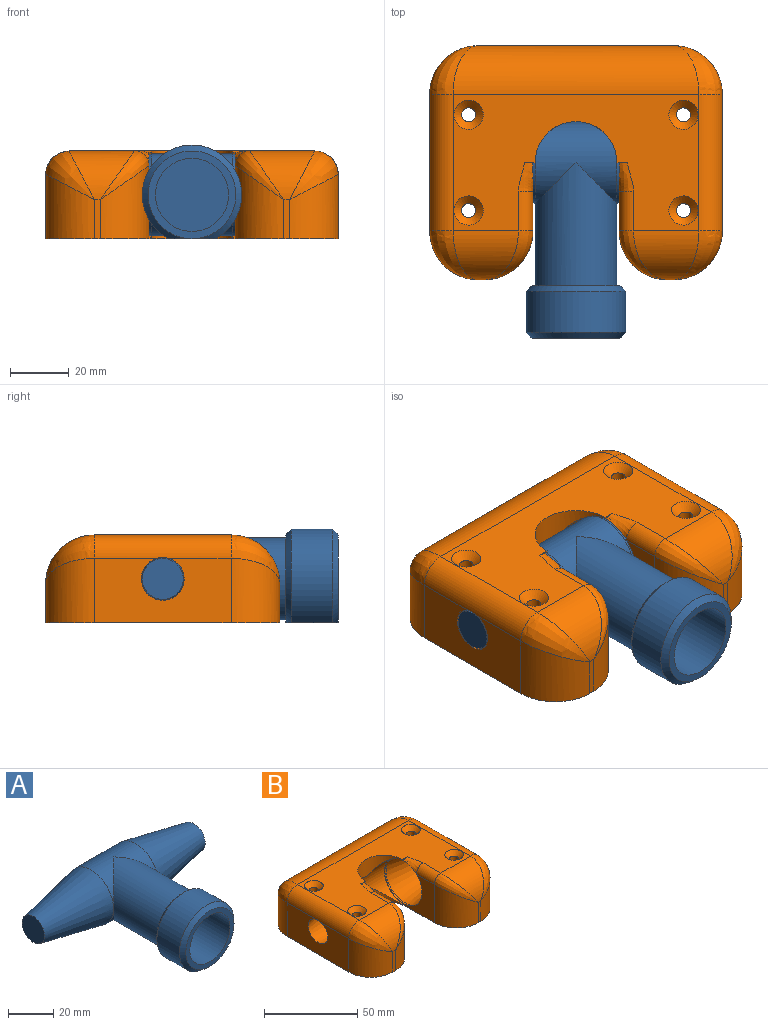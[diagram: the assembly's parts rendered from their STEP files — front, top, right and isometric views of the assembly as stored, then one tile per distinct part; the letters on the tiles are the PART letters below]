
ASSEMBLY  parts=2 mates=1
PART A: 14 faces, bbox 100x74x34 mm
  f0: cylinder r=17mm len=34mm, axis (0,1,0), area 1262.2mm2, adj f1,f2,f13
  f1: cone r=15mm half-angle=45deg, axis (0,-1,0), area 253.8mm2, adj f0,f10,f13
  f2: cone r=17mm half-angle=45deg, axis (0,1,0), area 253.8mm2, adj f0,f9,f13
  f3: cone r=7mm half-angle=11deg, axis (1,0,0), area 2419.5mm2, adj f4,f7
  f4: plane 14x14mm, normal (-1,0,0), area 153.9mm2, adj f3
  f5: plane 14x14mm, normal (1,0,0), area 153.9mm2, adj f6
  f6: cone r=7mm half-angle=11deg, axis (-1,0,0), area 2419.5mm2, adj f5,f7
  f7: cylinder r=14mm len=28mm, axis (-1,0,0), area 1679mm2, adj f3,f6,f8
  f8: cylinder r=14mm len=42mm, axis (0,1,0), area 2910.5mm2, adj f7,f10
  f9: plane 30x30mm, normal (0,-1,0), area 216mm2, adj f2,f11
  f10: plane 30x30mm, normal (0,1,0), area 91.1mm2, adj f1,f8
  f11: cylinder r=12.5mm len=34mm, axis (0,-1,0), area 2670.4mm2, adj f9,f12
  f12: plane 25x25mm, normal (0,-1,0), area 490.9mm2, adj f11
  f13: plane 18.01x16.02mm, normal (0,0,-1), area 266.1mm2, adj f0,f1,f2
PART B: 49 faces, bbox 100x80x30 mm
  f0: cylinder r=14mm len=28mm, axis (-1,0,0), area 76.7mm2, adj f13,f18,f45
  f1: cylinder r=14mm len=28mm, axis (0,0,1), area 222.5mm2, adj f2,f3,f5,f19
  f2: plane 3.71x1.01mm, normal (0,-1,0), area 1.3mm2, adj f1,f5,f13,f19,f45
  f3: plane 3.71x1.01mm, normal (0,-1,0), area 1.3mm2, adj f1,f5,f15,f19,f48
  f4: plane 13.34x1.98mm, normal (0,-1,0), area 26.5mm2, adj f11,f20,f21,f22
  f5: plane 84x46.68mm, normal (0,0,1), area 2398.4mm2, adj f1,f2,f3,f21,f24,f27,f30,f32
  f6: plane 46.68x22mm, normal (1,0,0), area 860.2mm2, adj f11,f16,f20,f28,f41
  f7: plane 66.68x13.34mm, normal (0,1,0), area 889.7mm2, adj f11,f26,f27,f28
  f8: plane 46.68x22mm, normal (-1,0,0), area 860.2mm2, adj f11,f18,f23,f26,f38
  f9: plane 13.34x1.98mm, normal (0,-1,0), area 26.5mm2, adj f11,f23,f24,f25
  f10: cylinder r=14mm len=28mm, axis (0,0,1), area 222.3mm2, adj f11,f12,f14,f19
  f11: plane 100x80mm, normal (0,0,-1), area 6086.4mm2, adj f4,f6,f7,f8,f9,f10,f12,f13
  f12: plane 0.7x0.5mm, normal (0,-1,0), area 0.3mm2, adj f10,f11,f13,f19
  f13: plane 37.84x29.5mm, normal (1,0,0), area 325mm2, adj f0,f2,f11,f12,f19,f25,f44
  f14: plane 0.7x0.5mm, normal (0,-1,0), area 0.3mm2, adj f10,f11,f15,f19
  f15: plane 37.84x29.5mm, normal (-1,0,0), area 325mm2, adj f3,f11,f14,f17,f19,f22,f47
  f16: cone r=7.29mm half-angle=11deg, axis (-1,0,0), area 2347.6mm2, adj f6,f17,f41
  f17: cylinder r=14mm len=28mm, axis (-1,0,0), area 76.7mm2, adj f15,f16,f48
  f18: cone r=7.29mm half-angle=11deg, axis (1,0,0), area 2347.6mm2, adj f0,f8,f38
  f19: cylinder r=14.5mm len=29.4mm, axis (-1,0,0), area 590.8mm2, adj f1,f2,f3,f10,f12,f13,f14,f15
  f20: cylinder r=16.66mm len=22mm, axis (0,0,1), area 493.3mm2, adj f4,f6,f11,f40
  f21: cylinder r=16.66mm len=22.3mm, axis (1,0,0), area 390.3mm2, adj f4,f5,f40,f46
  f22: cylinder r=16.66mm len=25mm, axis (0,0,-1), area 543.3mm2, adj f4,f11,f15,f46
  f23: cylinder r=16.66mm len=22mm, axis (0,0,-1), area 493.3mm2, adj f8,f9,f11,f37
  f24: cylinder r=16.66mm len=22.3mm, axis (1,0,0), area 390.3mm2, adj f5,f9,f37,f43
  f25: cylinder r=16.66mm len=25mm, axis (0,0,1), area 543.3mm2, adj f9,f11,f13,f43
  f26: cylinder r=16.66mm len=22mm, axis (0,0,1), area 493.3mm2, adj f7,f8,f11,f39
  f27: cylinder r=16.66mm len=84mm, axis (-1,0,0), area 2033.3mm2, adj f5,f7,f39,f42
  f28: cylinder r=16.66mm len=22mm, axis (0,0,-1), area 493.3mm2, adj f6,f7,f11,f42
  f29: cylinder r=2.4mm len=27.4mm, axis (0,0,1), area 413.2mm2, adj f11,f30
  f30: cone r=2.4mm half-angle=45deg, axis (0,0,1), area 85.5mm2, adj f5,f29
  f31: cylinder r=2.4mm len=27.4mm, axis (0,0,1), area 413.2mm2, adj f11,f32
  f32: cone r=2.4mm half-angle=45deg, axis (0,0,1), area 85.5mm2, adj f5,f31
  f33: cylinder r=2.4mm len=27.4mm, axis (0,0,1), area 413.2mm2, adj f11,f34
  f34: cone r=2.4mm half-angle=45deg, axis (0,0,1), area 85.5mm2, adj f5,f33
  f35: cylinder r=2.4mm len=27.4mm, axis (0,0,1), area 413.2mm2, adj f11,f36
  f36: cone r=2.4mm half-angle=45deg, axis (0,0,1), area 85.5mm2, adj f5,f35
  f37: bspline ~19.85x16.66mm, area 220.3mm2, adj f23,f24,f38
  f38: cylinder r=8mm len=46.68mm, axis (0,-1,0), area 585.8mm2, adj f5,f8,f18,f37,f39
  f39: bspline ~19.85x16.66mm, area 220.3mm2, adj f26,f27,f38
  f40: bspline ~19.85x16.66mm, area 220.3mm2, adj f20,f21,f41
  f41: cylinder r=8mm len=46.68mm, axis (0,1,0), area 585.8mm2, adj f5,f6,f16,f40,f42
  f42: bspline ~19.85x16.66mm, area 218.7mm2, adj f27,f28,f41
  f43: bspline ~19.47x16.66mm, area 140.1mm2, adj f24,f25,f44
  f44: cylinder r=5mm len=13.54mm, axis (0,1,0), area 106.4mm2, adj f5,f13,f43,f45
  f45: bspline ~12.33x5.28mm, area 48.4mm2, adj f0,f2,f5,f44
  f46: bspline ~19.47x16.66mm, area 140.1mm2, adj f21,f22,f47
  f47: cylinder r=5mm len=13.54mm, axis (0,-1,0), area 106.4mm2, adj f5,f15,f46,f48
  f48: bspline ~11.64x5.28mm, area 48.4mm2, adj f3,f5,f17,f47
PLACE A t=(-18.22,-37.16,-9.17)mm
PLACE B t=(-18.22,-37.16,-9.17)mm
MATE revolute A.f6 <-> B.f0  axis (1,0,0) through (31.78,-37.16,-9.17)mm
